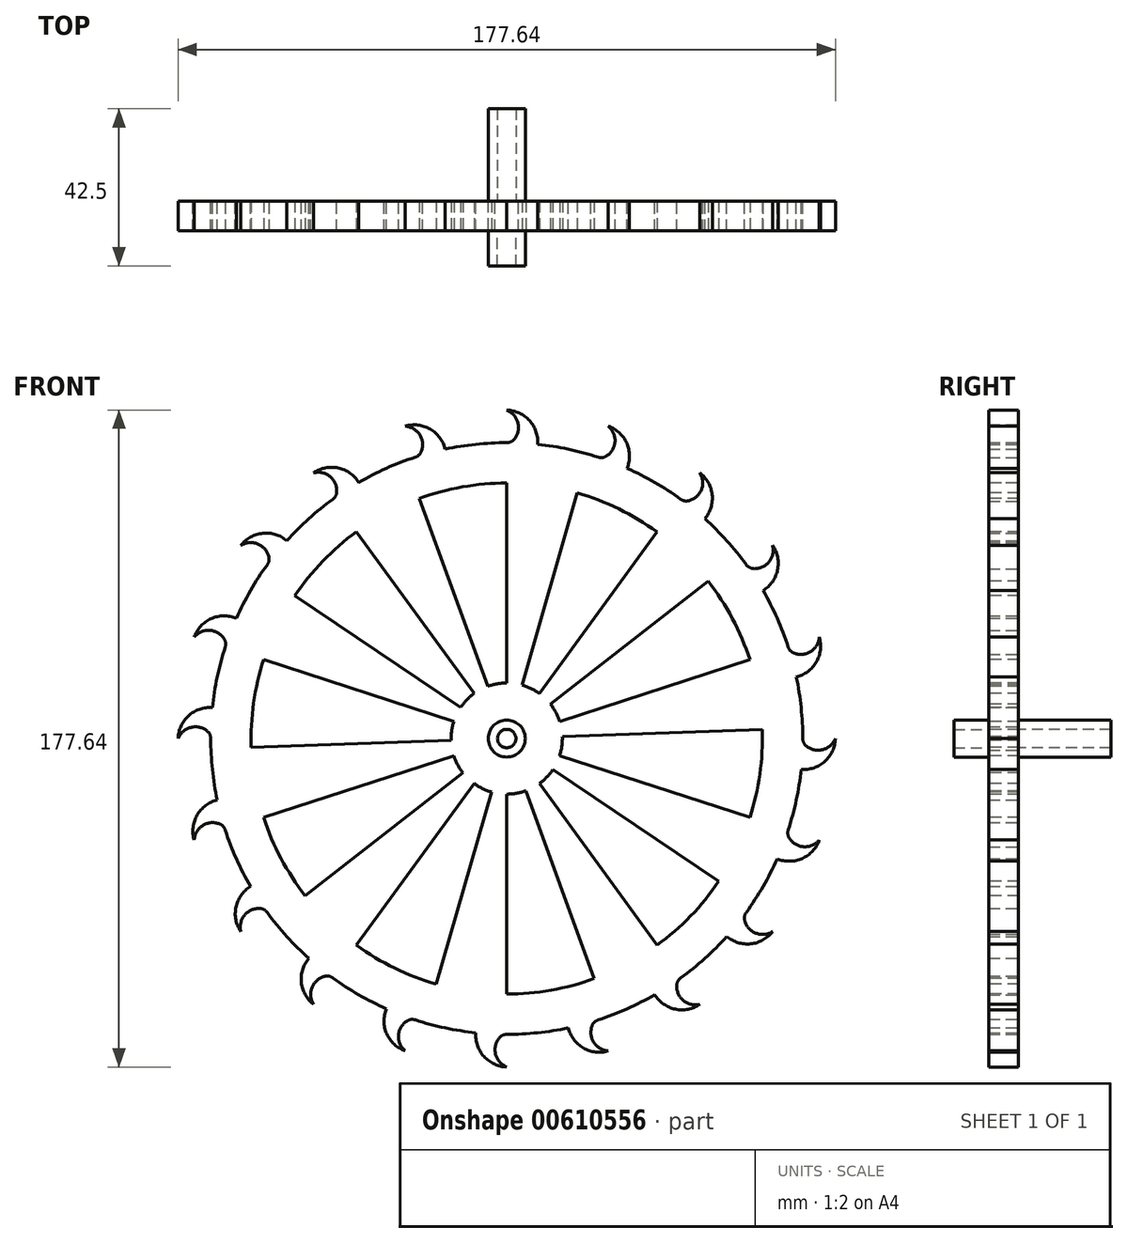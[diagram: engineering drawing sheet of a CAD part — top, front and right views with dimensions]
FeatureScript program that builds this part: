
annotation { "Feature Type Name" : "Feature", "Feature Type Description" : "" }
export const myFeature = defineFeature(function(context is Context, id is Id, definition is map)
    precondition{}
    {
        {
            var Q0;
            Q0=qCreatedBy(makeId("Front.planeOp"),FACE);
            var sketch = newSketch(context, id + "F0", { "sketchPlane" : qUnion([Q0])});
            skCircle(sketch, "E0", {"center": v(0, 0) * mm, "radius": 80 * mm});
            skArc(sketch, "E1", {"start": v(0, 80) * mm, "mid": v(1.13, 80.25) * mm, "end": v(2.04, 80.97) * mm});
            skLineSegment(sketch, "E2", {"start": v(0, 96.3) * mm, "end": v(0, 58.37) * mm, "construction": true});
            skArc(sketch, "E3", {"start": v(2.04, 80.97) * mm, "mid": v(3, 85.41) * mm, "end": v(0, 88.82) * mm});
            skArc(sketch, "E4", {"start": v(8.35, 79.56) * mm, "mid": v(6.16, 85.98) * mm, "end": v(0, 88.82) * mm});
            skArc(sketch, "E5.1.0", {"start": v(-16.64, 78.25) * mm, "mid": v(-20.71, 83.68) * mm, "end": v(-27.45, 84.47) * mm});
            skArc(sketch, "E5.1.1", {"start": v(-23.08, 77.64) * mm, "mid": v(-23.53, 82.16) * mm, "end": v(-27.45, 84.47) * mm});
            skArc(sketch, "E5.1.2", {"start": v(-24.72, 76.08) * mm, "mid": v(-23.73, 76.68) * mm, "end": v(-23.08, 77.64) * mm});
            skArc(sketch, "E5.2.0", {"start": v(-40, 69.28) * mm, "mid": v(-45.56, 73.18) * mm, "end": v(-52.2, 71.86) * mm});
            skArc(sketch, "E5.2.1", {"start": v(-45.94, 66.7) * mm, "mid": v(-47.77, 70.87) * mm, "end": v(-52.2, 71.86) * mm});
            skArc(sketch, "E5.2.2", {"start": v(-47.02, 64.72) * mm, "mid": v(-46.26, 65.6) * mm, "end": v(-45.94, 66.7) * mm});
            skArc(sketch, "E5.3.0", {"start": v(-59.46, 53.52) * mm, "mid": v(-65.94, 55.52) * mm, "end": v(-71.86, 52.2) * mm});
            skArc(sketch, "E5.3.1", {"start": v(-64.3, 49.24) * mm, "mid": v(-67.33, 52.64) * mm, "end": v(-71.86, 52.2) * mm});
            skArc(sketch, "E5.3.2", {"start": v(-64.72, 47.02) * mm, "mid": v(-64.26, 48.09) * mm, "end": v(-64.3, 49.24) * mm});
            skArc(sketch, "E5.4.0", {"start": v(-73.09, 32.53) * mm, "mid": v(-79.87, 32.43) * mm, "end": v(-84.47, 27.45) * mm});
            skArc(sketch, "E5.4.1", {"start": v(-76.38, 26.96) * mm, "mid": v(-80.3, 29.25) * mm, "end": v(-84.47, 27.45) * mm});
            skArc(sketch, "E5.4.2", {"start": v(-76.08, 24.72) * mm, "mid": v(-75.98, 25.87) * mm, "end": v(-76.38, 26.96) * mm});
            skArc(sketch, "E5.5.0", {"start": v(-79.56, 8.35) * mm, "mid": v(-85.98, 6.16) * mm, "end": v(-88.82, 0) * mm});
            skArc(sketch, "E5.5.1", {"start": v(-80.97, 2.04) * mm, "mid": v(-85.41, 3) * mm, "end": v(-88.82, 0) * mm});
            skArc(sketch, "E5.5.2", {"start": v(-80, 0) * mm, "mid": v(-80.25, 1.13) * mm, "end": v(-80.97, 2.04) * mm});
            skArc(sketch, "E5.6.0", {"start": v(-78.25, -16.64) * mm, "mid": v(-83.68, -20.71) * mm, "end": v(-84.47, -27.45) * mm});
            skArc(sketch, "E5.6.1", {"start": v(-77.64, -23.08) * mm, "mid": v(-82.16, -23.53) * mm, "end": v(-84.47, -27.45) * mm});
            skArc(sketch, "E5.6.2", {"start": v(-76.08, -24.72) * mm, "mid": v(-76.68, -23.73) * mm, "end": v(-77.64, -23.08) * mm});
            skArc(sketch, "E5.7.0", {"start": v(-69.28, -40) * mm, "mid": v(-73.18, -45.56) * mm, "end": v(-71.86, -52.2) * mm});
            skArc(sketch, "E5.7.1", {"start": v(-66.7, -45.94) * mm, "mid": v(-70.87, -47.77) * mm, "end": v(-71.86, -52.2) * mm});
            skArc(sketch, "E5.7.2", {"start": v(-64.72, -47.02) * mm, "mid": v(-65.6, -46.26) * mm, "end": v(-66.7, -45.94) * mm});
            skArc(sketch, "E5.8.0", {"start": v(-53.52, -59.46) * mm, "mid": v(-55.52, -65.94) * mm, "end": v(-52.2, -71.86) * mm});
            skArc(sketch, "E5.8.1", {"start": v(-49.24, -64.3) * mm, "mid": v(-52.64, -67.33) * mm, "end": v(-52.2, -71.86) * mm});
            skArc(sketch, "E5.8.2", {"start": v(-47.02, -64.72) * mm, "mid": v(-48.09, -64.26) * mm, "end": v(-49.24, -64.3) * mm});
            skArc(sketch, "E5.9.0", {"start": v(-32.53, -73.09) * mm, "mid": v(-32.43, -79.87) * mm, "end": v(-27.45, -84.47) * mm});
            skArc(sketch, "E5.9.1", {"start": v(-26.96, -76.38) * mm, "mid": v(-29.25, -80.3) * mm, "end": v(-27.45, -84.47) * mm});
            skArc(sketch, "E5.9.2", {"start": v(-24.72, -76.08) * mm, "mid": v(-25.87, -75.98) * mm, "end": v(-26.96, -76.38) * mm});
            skArc(sketch, "E5.10.0", {"start": v(-8.35, -79.56) * mm, "mid": v(-6.16, -85.98) * mm, "end": v(0, -88.82) * mm});
            skArc(sketch, "E5.10.1", {"start": v(-2.04, -80.97) * mm, "mid": v(-3, -85.41) * mm, "end": v(0, -88.82) * mm});
            skArc(sketch, "E5.10.2", {"start": v(0, -80) * mm, "mid": v(-1.13, -80.25) * mm, "end": v(-2.04, -80.97) * mm});
            skArc(sketch, "E5.11.0", {"start": v(16.64, -78.25) * mm, "mid": v(20.71, -83.68) * mm, "end": v(27.45, -84.47) * mm});
            skArc(sketch, "E5.11.1", {"start": v(23.08, -77.64) * mm, "mid": v(23.53, -82.16) * mm, "end": v(27.45, -84.47) * mm});
            skArc(sketch, "E5.11.2", {"start": v(24.72, -76.08) * mm, "mid": v(23.73, -76.68) * mm, "end": v(23.08, -77.64) * mm});
            skArc(sketch, "E5.12.0", {"start": v(40, -69.28) * mm, "mid": v(45.56, -73.18) * mm, "end": v(52.2, -71.86) * mm});
            skArc(sketch, "E5.12.1", {"start": v(45.94, -66.7) * mm, "mid": v(47.77, -70.87) * mm, "end": v(52.2, -71.86) * mm});
            skArc(sketch, "E5.12.2", {"start": v(47.02, -64.72) * mm, "mid": v(46.26, -65.6) * mm, "end": v(45.94, -66.7) * mm});
            skArc(sketch, "E5.13.0", {"start": v(59.46, -53.52) * mm, "mid": v(65.94, -55.52) * mm, "end": v(71.86, -52.2) * mm});
            skArc(sketch, "E5.13.1", {"start": v(64.3, -49.24) * mm, "mid": v(67.33, -52.64) * mm, "end": v(71.86, -52.2) * mm});
            skArc(sketch, "E5.13.2", {"start": v(64.72, -47.02) * mm, "mid": v(64.26, -48.09) * mm, "end": v(64.3, -49.24) * mm});
            skArc(sketch, "E5.14.0", {"start": v(73.09, -32.53) * mm, "mid": v(79.87, -32.43) * mm, "end": v(84.47, -27.45) * mm});
            skArc(sketch, "E5.14.1", {"start": v(76.38, -26.96) * mm, "mid": v(80.3, -29.25) * mm, "end": v(84.47, -27.45) * mm});
            skArc(sketch, "E5.14.2", {"start": v(76.08, -24.72) * mm, "mid": v(75.98, -25.87) * mm, "end": v(76.38, -26.96) * mm});
            skArc(sketch, "E5.15.0", {"start": v(79.56, -8.35) * mm, "mid": v(85.98, -6.16) * mm, "end": v(88.82, 0) * mm});
            skArc(sketch, "E5.15.1", {"start": v(80.97, -2.04) * mm, "mid": v(85.41, -3) * mm, "end": v(88.82, 0) * mm});
            skArc(sketch, "E5.15.2", {"start": v(80, 0) * mm, "mid": v(80.25, -1.13) * mm, "end": v(80.97, -2.04) * mm});
            skArc(sketch, "E5.16.0", {"start": v(78.25, 16.64) * mm, "mid": v(83.68, 20.71) * mm, "end": v(84.47, 27.45) * mm});
            skArc(sketch, "E5.16.1", {"start": v(77.64, 23.08) * mm, "mid": v(82.16, 23.53) * mm, "end": v(84.47, 27.45) * mm});
            skArc(sketch, "E5.16.2", {"start": v(76.08, 24.72) * mm, "mid": v(76.68, 23.73) * mm, "end": v(77.64, 23.08) * mm});
            skArc(sketch, "E5.17.0", {"start": v(69.28, 40) * mm, "mid": v(73.18, 45.56) * mm, "end": v(71.86, 52.2) * mm});
            skArc(sketch, "E5.17.1", {"start": v(66.7, 45.94) * mm, "mid": v(70.87, 47.77) * mm, "end": v(71.86, 52.2) * mm});
            skArc(sketch, "E5.17.2", {"start": v(64.72, 47.02) * mm, "mid": v(65.6, 46.26) * mm, "end": v(66.7, 45.94) * mm});
            skArc(sketch, "E5.18.0", {"start": v(53.52, 59.46) * mm, "mid": v(55.52, 65.94) * mm, "end": v(52.2, 71.86) * mm});
            skArc(sketch, "E5.18.1", {"start": v(49.24, 64.3) * mm, "mid": v(52.64, 67.33) * mm, "end": v(52.2, 71.86) * mm});
            skArc(sketch, "E5.18.2", {"start": v(47.02, 64.72) * mm, "mid": v(48.09, 64.26) * mm, "end": v(49.24, 64.3) * mm});
            skArc(sketch, "E5.19.0", {"start": v(32.53, 73.09) * mm, "mid": v(32.43, 79.87) * mm, "end": v(27.45, 84.47) * mm});
            skArc(sketch, "E5.19.1", {"start": v(26.96, 76.38) * mm, "mid": v(29.25, 80.3) * mm, "end": v(27.45, 84.47) * mm});
            skArc(sketch, "E5.19.2", {"start": v(24.72, 76.08) * mm, "mid": v(25.87, 75.98) * mm, "end": v(26.96, 76.38) * mm});
            skSolve(sketch);
        }
        {
            var Q0;
            {var subQ0=sQuery(id+"F0.wireOp",EDGE,"E5.19.0");Q0=makeQuery(id+"F0.imprint","IMPRINT",FACE,{"disambiguationData":[TD([[makeQuery(id+"F0.imprint","IMPRINT",EDGE,{"derivedFrom":subQ0}),1.0]])]});}
            var Q1;
            {var subQ0=sQuery(id+"F0.wireOp",EDGE,"E0");var subQ18=makeQuery(id+"F0.imprint","INTERSECT",VERTEX,{"derivedFrom":[sQuery(id+"F0.wireOp",EDGE,"E5.14.2"),subQ0]});Q1=makeQuery(id+"F0.imprint","IMPRINT",FACE,{"disambiguationData":[TD([[makeQuery(id+"F0.imprint","IMPRINT",EDGE,{"disambiguationData":[TD([[subQ18,-1.0]])],"derivedFrom":subQ0}),1.0]])]});}
            var Q2;
            {var subQ0=sQuery(id+"F0.wireOp",EDGE,"E5.15.0");Q2=makeQuery(id+"F0.imprint","IMPRINT",FACE,{"disambiguationData":[TD([[makeQuery(id+"F0.imprint","IMPRINT",EDGE,{"derivedFrom":subQ0}),1.0]])]});}
            var Q3;
            {var subQ0=sQuery(id+"F0.wireOp",EDGE,"E5.13.0");Q3=makeQuery(id+"F0.imprint","IMPRINT",FACE,{"disambiguationData":[TD([[makeQuery(id+"F0.imprint","IMPRINT",EDGE,{"derivedFrom":subQ0}),1.0]])]});}
            var Q4;
            {var subQ0=sQuery(id+"F0.wireOp",EDGE,"E5.16.0");Q4=makeQuery(id+"F0.imprint","IMPRINT",FACE,{"disambiguationData":[TD([[makeQuery(id+"F0.imprint","IMPRINT",EDGE,{"derivedFrom":subQ0}),1.0]])]});}
            var Q5;
            {var subQ0=sQuery(id+"F0.wireOp",EDGE,"E5.14.0");Q5=makeQuery(id+"F0.imprint","IMPRINT",FACE,{"disambiguationData":[TD([[makeQuery(id+"F0.imprint","IMPRINT",EDGE,{"derivedFrom":subQ0}),1.0]])]});}
            var Q6;
            {var subQ0=sQuery(id+"F0.wireOp",EDGE,"E1");Q6=makeQuery(id+"F0.imprint","IMPRINT",FACE,{"disambiguationData":[TD([[makeQuery(id+"F0.imprint","IMPRINT",EDGE,{"derivedFrom":subQ0}),-1.0]])]});}
            var Q7;
            {var subQ0=sQuery(id+"F0.wireOp",EDGE,"E5.1.0");Q7=makeQuery(id+"F0.imprint","IMPRINT",FACE,{"disambiguationData":[TD([[makeQuery(id+"F0.imprint","IMPRINT",EDGE,{"derivedFrom":subQ0}),1.0]])]});}
            var Q8;
            {var subQ0=sQuery(id+"F0.wireOp",EDGE,"E5.2.0");Q8=makeQuery(id+"F0.imprint","IMPRINT",FACE,{"disambiguationData":[TD([[makeQuery(id+"F0.imprint","IMPRINT",EDGE,{"derivedFrom":subQ0}),1.0]])]});}
            var Q9;
            {var subQ0=sQuery(id+"F0.wireOp",EDGE,"E5.3.0");Q9=makeQuery(id+"F0.imprint","IMPRINT",FACE,{"disambiguationData":[TD([[makeQuery(id+"F0.imprint","IMPRINT",EDGE,{"derivedFrom":subQ0}),1.0]])]});}
            var Q10;
            {var subQ0=sQuery(id+"F0.wireOp",EDGE,"E5.4.0");Q10=makeQuery(id+"F0.imprint","IMPRINT",FACE,{"disambiguationData":[TD([[makeQuery(id+"F0.imprint","IMPRINT",EDGE,{"derivedFrom":subQ0}),1.0]])]});}
            var Q11;
            {var subQ0=sQuery(id+"F0.wireOp",EDGE,"E5.5.0");Q11=makeQuery(id+"F0.imprint","IMPRINT",FACE,{"disambiguationData":[TD([[makeQuery(id+"F0.imprint","IMPRINT",EDGE,{"derivedFrom":subQ0}),1.0]])]});}
            var Q12;
            {var subQ0=sQuery(id+"F0.wireOp",EDGE,"E5.6.0");Q12=makeQuery(id+"F0.imprint","IMPRINT",FACE,{"disambiguationData":[TD([[makeQuery(id+"F0.imprint","IMPRINT",EDGE,{"derivedFrom":subQ0}),1.0]])]});}
            var Q13;
            {var subQ0=sQuery(id+"F0.wireOp",EDGE,"E5.7.0");Q13=makeQuery(id+"F0.imprint","IMPRINT",FACE,{"disambiguationData":[TD([[makeQuery(id+"F0.imprint","IMPRINT",EDGE,{"derivedFrom":subQ0}),1.0]])]});}
            var Q14;
            {var subQ0=sQuery(id+"F0.wireOp",EDGE,"E5.8.0");Q14=makeQuery(id+"F0.imprint","IMPRINT",FACE,{"disambiguationData":[TD([[makeQuery(id+"F0.imprint","IMPRINT",EDGE,{"derivedFrom":subQ0}),1.0]])]});}
            var Q15;
            {var subQ0=sQuery(id+"F0.wireOp",EDGE,"E5.9.0");Q15=makeQuery(id+"F0.imprint","IMPRINT",FACE,{"disambiguationData":[TD([[makeQuery(id+"F0.imprint","IMPRINT",EDGE,{"derivedFrom":subQ0}),1.0]])]});}
            var Q16;
            {var subQ0=sQuery(id+"F0.wireOp",EDGE,"E5.10.0");Q16=makeQuery(id+"F0.imprint","IMPRINT",FACE,{"disambiguationData":[TD([[makeQuery(id+"F0.imprint","IMPRINT",EDGE,{"derivedFrom":subQ0}),1.0]])]});}
            var Q17;
            {var subQ0=sQuery(id+"F0.wireOp",EDGE,"E5.11.0");Q17=makeQuery(id+"F0.imprint","IMPRINT",FACE,{"disambiguationData":[TD([[makeQuery(id+"F0.imprint","IMPRINT",EDGE,{"derivedFrom":subQ0}),1.0]])]});}
            var Q18;
            {var subQ0=sQuery(id+"F0.wireOp",EDGE,"E5.12.0");Q18=makeQuery(id+"F0.imprint","IMPRINT",FACE,{"disambiguationData":[TD([[makeQuery(id+"F0.imprint","IMPRINT",EDGE,{"derivedFrom":subQ0}),1.0]])]});}
            var Q19;
            {var subQ0=sQuery(id+"F0.wireOp",EDGE,"E5.17.0");Q19=makeQuery(id+"F0.imprint","IMPRINT",FACE,{"disambiguationData":[TD([[makeQuery(id+"F0.imprint","IMPRINT",EDGE,{"derivedFrom":subQ0}),1.0]])]});}
            var Q20;
            {var subQ0=sQuery(id+"F0.wireOp",EDGE,"E5.18.0");Q20=makeQuery(id+"F0.imprint","IMPRINT",FACE,{"disambiguationData":[TD([[makeQuery(id+"F0.imprint","IMPRINT",EDGE,{"derivedFrom":subQ0}),1.0]])]});}
            extrude(context, id + "F1", {"entities" : qUnion([Q0, Q1, Q2, Q3, Q4, Q5, Q6, Q7, Q8, Q9, Q10, Q11, Q12, Q13, Q14, Q15, Q16, Q17, Q18, Q19, Q20]), "depth" : 8 * mm, "offsetDistance" : 25 * mm});
        }
        {
            var Q0;
            Q0=makeQuery(id+"F1.opExtrude","CAP_FACE",FACE,{"disambiguationData":[OSD([sQuery(id+"F0.wireOp",EDGE,"E1"),sQuery(id+"F0.wireOp",EDGE,"E3"),sQuery(id+"F0.wireOp",EDGE,"E4"),sQuery(id+"F0.wireOp",EDGE,"E5.1.0"),sQuery(id+"F0.wireOp",EDGE,"E5.1.1"),sQuery(id+"F0.wireOp",EDGE,"E5.1.2"),sQuery(id+"F0.wireOp",EDGE,"E5.2.0"),sQuery(id+"F0.wireOp",EDGE,"E5.2.1"),sQuery(id+"F0.wireOp",EDGE,"E5.2.2"),sQuery(id+"F0.wireOp",EDGE,"E5.3.0"),sQuery(id+"F0.wireOp",EDGE,"E5.3.1"),sQuery(id+"F0.wireOp",EDGE,"E5.3.2"),sQuery(id+"F0.wireOp",EDGE,"E5.4.0"),sQuery(id+"F0.wireOp",EDGE,"E5.4.1"),sQuery(id+"F0.wireOp",EDGE,"E5.4.2"),sQuery(id+"F0.wireOp",EDGE,"E5.5.0"),sQuery(id+"F0.wireOp",EDGE,"E5.5.1"),sQuery(id+"F0.wireOp",EDGE,"E5.5.2"),sQuery(id+"F0.wireOp",EDGE,"E5.6.0"),sQuery(id+"F0.wireOp",EDGE,"E5.6.1"),sQuery(id+"F0.wireOp",EDGE,"E5.6.2"),sQuery(id+"F0.wireOp",EDGE,"E5.7.0"),sQuery(id+"F0.wireOp",EDGE,"E5.7.1"),sQuery(id+"F0.wireOp",EDGE,"E5.7.2"),sQuery(id+"F0.wireOp",EDGE,"E5.8.0"),sQuery(id+"F0.wireOp",EDGE,"E5.8.1"),sQuery(id+"F0.wireOp",EDGE,"E5.8.2"),sQuery(id+"F0.wireOp",EDGE,"E5.9.0"),sQuery(id+"F0.wireOp",EDGE,"E5.9.1"),sQuery(id+"F0.wireOp",EDGE,"E5.9.2"),sQuery(id+"F0.wireOp",EDGE,"E5.10.0"),sQuery(id+"F0.wireOp",EDGE,"E5.10.1"),sQuery(id+"F0.wireOp",EDGE,"E5.10.2"),sQuery(id+"F0.wireOp",EDGE,"E5.11.0"),sQuery(id+"F0.wireOp",EDGE,"E5.11.1"),sQuery(id+"F0.wireOp",EDGE,"E5.11.2"),sQuery(id+"F0.wireOp",EDGE,"E5.12.0"),sQuery(id+"F0.wireOp",EDGE,"E5.12.1"),sQuery(id+"F0.wireOp",EDGE,"E5.12.2"),sQuery(id+"F0.wireOp",EDGE,"E5.13.0"),sQuery(id+"F0.wireOp",EDGE,"E5.13.1"),sQuery(id+"F0.wireOp",EDGE,"E5.13.2"),sQuery(id+"F0.wireOp",EDGE,"E5.14.0"),sQuery(id+"F0.wireOp",EDGE,"E5.14.1"),sQuery(id+"F0.wireOp",EDGE,"E5.14.2"),sQuery(id+"F0.wireOp",EDGE,"E5.15.0"),sQuery(id+"F0.wireOp",EDGE,"E5.15.1"),sQuery(id+"F0.wireOp",EDGE,"E5.15.2"),sQuery(id+"F0.wireOp",EDGE,"E5.16.0"),sQuery(id+"F0.wireOp",EDGE,"E5.16.1"),sQuery(id+"F0.wireOp",EDGE,"E5.16.2"),sQuery(id+"F0.wireOp",EDGE,"E5.17.0"),sQuery(id+"F0.wireOp",EDGE,"E5.17.1"),sQuery(id+"F0.wireOp",EDGE,"E5.17.2"),sQuery(id+"F0.wireOp",EDGE,"E5.18.0"),sQuery(id+"F0.wireOp",EDGE,"E5.18.1"),sQuery(id+"F0.wireOp",EDGE,"E5.18.2"),sQuery(id+"F0.wireOp",EDGE,"E5.19.0"),sQuery(id+"F0.wireOp",EDGE,"E5.19.1"),sQuery(id+"F0.wireOp",EDGE,"E5.19.2"),sQuery(id+"F0.wireOp",EDGE,"E0")])],"isStart":false});
            var sketch = newSketch(context, id + "F2", { "sketchPlane" : qUnion([Q0])});
            skArc(sketch, "E6", {"start": v(-5.14, 14.13) * mm, "mid": v(-2.61, 14.8) * mm, "end": v(0, 15.04) * mm});
            skArc(sketch, "E7", {"start": v(0, 69.1) * mm, "mid": v(-12, 68.04) * mm, "end": v(-23.63, 64.92) * mm});
            skLineSegment(sketch, "E8", {"start": v(0, 69.1) * mm, "end": v(0, 15.04) * mm});
            skLineSegment(sketch, "E9", {"start": v(-23.63, 64.92) * mm, "end": v(-5.14, 14.13) * mm});
            skArc(sketch, "E10.1.0", {"start": v(-12.47, 8.4) * mm, "mid": v(-10.82, 10.45) * mm, "end": v(-8.84, 12.16) * mm});
            skLineSegment(sketch, "E10.1.1", {"start": v(-57.28, 38.63) * mm, "end": v(-12.47, 8.4) * mm});
            skLineSegment(sketch, "E10.1.2", {"start": v(-40.61, 55.9) * mm, "end": v(-8.84, 12.16) * mm});
            skArc(sketch, "E10.1.3", {"start": v(-40.61, 55.9) * mm, "mid": v(-49.7, 48) * mm, "end": v(-57.28, 38.63) * mm});
            skArc(sketch, "E10.2.0", {"start": v(-15.03, -0.52) * mm, "mid": v(-14.9, 2.1) * mm, "end": v(-14.3, 4.65) * mm});
            skLineSegment(sketch, "E10.2.1", {"start": v(-69.05, -2.41) * mm, "end": v(-15.03, -0.52) * mm});
            skLineSegment(sketch, "E10.2.2", {"start": v(-65.7, 21.35) * mm, "end": v(-14.3, 4.65) * mm});
            skArc(sketch, "E10.2.3", {"start": v(-65.7, 21.35) * mm, "mid": v(-68.42, 9.62) * mm, "end": v(-69.05, -2.41) * mm});
            skArc(sketch, "E10.3.0", {"start": v(-11.85, -9.26) * mm, "mid": v(-13.28, -7.06) * mm, "end": v(-14.3, -4.65) * mm});
            skLineSegment(sketch, "E10.3.1", {"start": v(-54.44, -42.54) * mm, "end": v(-11.85, -9.26) * mm});
            skLineSegment(sketch, "E10.3.2", {"start": v(-65.7, -21.35) * mm, "end": v(-14.3, -4.65) * mm});
            skArc(sketch, "E10.3.3", {"start": v(-65.7, -21.35) * mm, "mid": v(-61, -32.44) * mm, "end": v(-54.44, -42.54) * mm});
            skArc(sketch, "E10.4.0", {"start": v(-4.14, -14.45) * mm, "mid": v(-6.6, -13.51) * mm, "end": v(-8.84, -12.16) * mm});
            skLineSegment(sketch, "E10.4.1", {"start": v(-19.04, -66.41) * mm, "end": v(-4.14, -14.45) * mm});
            skLineSegment(sketch, "E10.4.2", {"start": v(-40.61, -55.9) * mm, "end": v(-8.84, -12.16) * mm});
            skArc(sketch, "E10.4.3", {"start": v(-40.61, -55.9) * mm, "mid": v(-30.29, -62.1) * mm, "end": v(-19.04, -66.41) * mm});
            skArc(sketch, "E10.5.0", {"start": v(5.14, -14.13) * mm, "mid": v(2.61, -14.8) * mm, "end": v(0, -15.04) * mm});
            skLineSegment(sketch, "E10.5.1", {"start": v(23.63, -64.92) * mm, "end": v(5.14, -14.13) * mm});
            skLineSegment(sketch, "E10.5.2", {"start": v(0, -69.1) * mm, "end": v(0, -15.04) * mm});
            skArc(sketch, "E10.5.3", {"start": v(0, -69.1) * mm, "mid": v(12, -68.04) * mm, "end": v(23.63, -64.92) * mm});
            skArc(sketch, "E10.6.0", {"start": v(12.47, -8.4) * mm, "mid": v(10.82, -10.45) * mm, "end": v(8.84, -12.16) * mm});
            skLineSegment(sketch, "E10.6.1", {"start": v(57.28, -38.63) * mm, "end": v(12.47, -8.4) * mm});
            skLineSegment(sketch, "E10.6.2", {"start": v(40.61, -55.9) * mm, "end": v(8.84, -12.16) * mm});
            skArc(sketch, "E10.6.3", {"start": v(40.61, -55.9) * mm, "mid": v(49.7, -48) * mm, "end": v(57.28, -38.63) * mm});
            skArc(sketch, "E10.7.0", {"start": v(15.03, 0.52) * mm, "mid": v(14.9, -2.1) * mm, "end": v(14.3, -4.65) * mm});
            skLineSegment(sketch, "E10.7.1", {"start": v(69.05, 2.41) * mm, "end": v(15.03, 0.52) * mm});
            skLineSegment(sketch, "E10.7.2", {"start": v(65.7, -21.35) * mm, "end": v(14.3, -4.65) * mm});
            skArc(sketch, "E10.7.3", {"start": v(65.7, -21.35) * mm, "mid": v(68.42, -9.62) * mm, "end": v(69.05, 2.41) * mm});
            skArc(sketch, "E10.8.0", {"start": v(11.85, 9.26) * mm, "mid": v(13.28, 7.06) * mm, "end": v(14.3, 4.65) * mm});
            skLineSegment(sketch, "E10.8.1", {"start": v(54.44, 42.54) * mm, "end": v(11.85, 9.26) * mm});
            skLineSegment(sketch, "E10.8.2", {"start": v(65.7, 21.35) * mm, "end": v(14.3, 4.65) * mm});
            skArc(sketch, "E10.8.3", {"start": v(65.7, 21.35) * mm, "mid": v(61, 32.44) * mm, "end": v(54.44, 42.54) * mm});
            skArc(sketch, "E10.9.0", {"start": v(4.14, 14.45) * mm, "mid": v(6.6, 13.51) * mm, "end": v(8.84, 12.16) * mm});
            skLineSegment(sketch, "E10.9.1", {"start": v(19.04, 66.41) * mm, "end": v(4.14, 14.45) * mm});
            skLineSegment(sketch, "E10.9.2", {"start": v(40.61, 55.9) * mm, "end": v(8.84, 12.16) * mm});
            skArc(sketch, "E10.9.3", {"start": v(40.61, 55.9) * mm, "mid": v(30.29, 62.1) * mm, "end": v(19.04, 66.41) * mm});
            skSolve(sketch);
        }
        {
            var Q0;
            Q0 = qSketchRegion(id + "F2", true);
            extrude(context, id + "F3", {"entities" : qUnion([Q0]), "operationType" : NewBodyOperationType.REMOVE, "oppositeDirection" : true, "depth" : 25 * mm, "offsetDistance" : 25 * mm});
        }
        {
            var Q0;
            Q0=makeQuery(id+"F1.opExtrude","CAP_FACE",FACE,{"disambiguationData":[OSD([sQuery(id+"F0.wireOp",EDGE,"E1"),sQuery(id+"F0.wireOp",EDGE,"E3"),sQuery(id+"F0.wireOp",EDGE,"E4"),sQuery(id+"F0.wireOp",EDGE,"E5.1.0"),sQuery(id+"F0.wireOp",EDGE,"E5.1.1"),sQuery(id+"F0.wireOp",EDGE,"E5.1.2"),sQuery(id+"F0.wireOp",EDGE,"E5.2.0"),sQuery(id+"F0.wireOp",EDGE,"E5.2.1"),sQuery(id+"F0.wireOp",EDGE,"E5.2.2"),sQuery(id+"F0.wireOp",EDGE,"E5.3.0"),sQuery(id+"F0.wireOp",EDGE,"E5.3.1"),sQuery(id+"F0.wireOp",EDGE,"E5.3.2"),sQuery(id+"F0.wireOp",EDGE,"E5.4.0"),sQuery(id+"F0.wireOp",EDGE,"E5.4.1"),sQuery(id+"F0.wireOp",EDGE,"E5.4.2"),sQuery(id+"F0.wireOp",EDGE,"E5.5.0"),sQuery(id+"F0.wireOp",EDGE,"E5.5.1"),sQuery(id+"F0.wireOp",EDGE,"E5.5.2"),sQuery(id+"F0.wireOp",EDGE,"E5.6.0"),sQuery(id+"F0.wireOp",EDGE,"E5.6.1"),sQuery(id+"F0.wireOp",EDGE,"E5.6.2"),sQuery(id+"F0.wireOp",EDGE,"E5.7.0"),sQuery(id+"F0.wireOp",EDGE,"E5.7.1"),sQuery(id+"F0.wireOp",EDGE,"E5.7.2"),sQuery(id+"F0.wireOp",EDGE,"E5.8.0"),sQuery(id+"F0.wireOp",EDGE,"E5.8.1"),sQuery(id+"F0.wireOp",EDGE,"E5.8.2"),sQuery(id+"F0.wireOp",EDGE,"E5.9.0"),sQuery(id+"F0.wireOp",EDGE,"E5.9.1"),sQuery(id+"F0.wireOp",EDGE,"E5.9.2"),sQuery(id+"F0.wireOp",EDGE,"E5.10.0"),sQuery(id+"F0.wireOp",EDGE,"E5.10.1"),sQuery(id+"F0.wireOp",EDGE,"E5.10.2"),sQuery(id+"F0.wireOp",EDGE,"E5.11.0"),sQuery(id+"F0.wireOp",EDGE,"E5.11.1"),sQuery(id+"F0.wireOp",EDGE,"E5.11.2"),sQuery(id+"F0.wireOp",EDGE,"E5.12.0"),sQuery(id+"F0.wireOp",EDGE,"E5.12.1"),sQuery(id+"F0.wireOp",EDGE,"E5.12.2"),sQuery(id+"F0.wireOp",EDGE,"E5.13.0"),sQuery(id+"F0.wireOp",EDGE,"E5.13.1"),sQuery(id+"F0.wireOp",EDGE,"E5.13.2"),sQuery(id+"F0.wireOp",EDGE,"E5.14.0"),sQuery(id+"F0.wireOp",EDGE,"E5.14.1"),sQuery(id+"F0.wireOp",EDGE,"E5.14.2"),sQuery(id+"F0.wireOp",EDGE,"E5.15.0"),sQuery(id+"F0.wireOp",EDGE,"E5.15.1"),sQuery(id+"F0.wireOp",EDGE,"E5.15.2"),sQuery(id+"F0.wireOp",EDGE,"E5.16.0"),sQuery(id+"F0.wireOp",EDGE,"E5.16.1"),sQuery(id+"F0.wireOp",EDGE,"E5.16.2"),sQuery(id+"F0.wireOp",EDGE,"E5.17.0"),sQuery(id+"F0.wireOp",EDGE,"E5.17.1"),sQuery(id+"F0.wireOp",EDGE,"E5.17.2"),sQuery(id+"F0.wireOp",EDGE,"E5.18.0"),sQuery(id+"F0.wireOp",EDGE,"E5.18.1"),sQuery(id+"F0.wireOp",EDGE,"E5.18.2"),sQuery(id+"F0.wireOp",EDGE,"E5.19.0"),sQuery(id+"F0.wireOp",EDGE,"E5.19.1"),sQuery(id+"F0.wireOp",EDGE,"E5.19.2"),sQuery(id+"F0.wireOp",EDGE,"E0")])],"isStart":false});
            var sketch = newSketch(context, id + "F4", { "sketchPlane" : qUnion([Q0])});
            skCircle(sketch, "E11", {"center": v(0, 0) * mm, "radius": 5 * mm});
            skCircle(sketch, "E12", {"center": v(0, 0) * mm, "radius": 2.5 * mm});
            skSolve(sketch);
        }
        {
            var Q0;
            Q0 = qSketchRegion(id + "F4", true);
            extrude(context, id + "F5", {"entities" : qUnion([Q0]), "operationType" : NewBodyOperationType.ADD, "depth" : 9.5 * mm, "offsetDistance" : 25 * mm});
        }
        {
            var Q0;
            Q0 = qSketchRegion(id + "F4", true);
            extrude(context, id + "F6", {"entities" : qUnion([Q0]), "operationType" : NewBodyOperationType.ADD, "oppositeDirection" : true, "depth" : 33 * mm, "offsetDistance" : 25 * mm});
        }
    });
